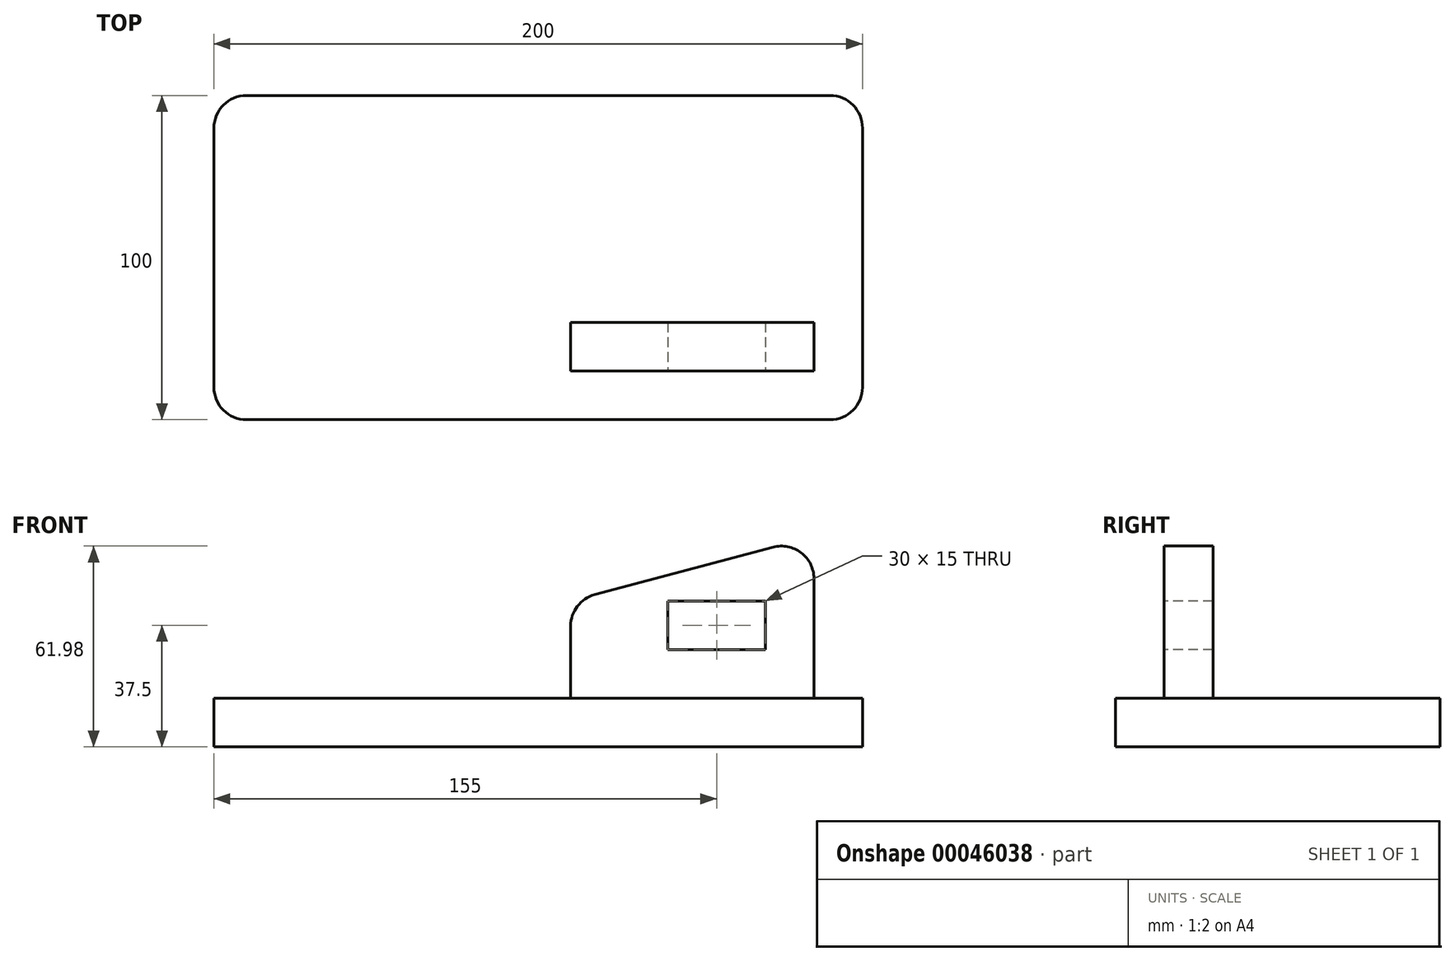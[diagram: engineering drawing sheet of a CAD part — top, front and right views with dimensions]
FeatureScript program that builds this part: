
annotation { "Feature Type Name" : "Feature", "Feature Type Description" : "" }
export const myFeature = defineFeature(function(context is Context, id is Id, definition is map)
    precondition{}
    {
        {
            var Q0;
            Q0=qCreatedBy(makeId("Top.planeOp"),FACE);
            var sketch = newSketch(context, id + "F0", { "sketchPlane" : qUnion([Q0])});
            skLineSegment(sketch, "E0.rect.bottom", {"start": v(100, -50) * mm, "end": v(-100, -50) * mm});
            skLineSegment(sketch, "E0.rect.top", {"start": v(100, 50) * mm, "end": v(-100, 50) * mm});
            skLineSegment(sketch, "E0.rect.left", {"start": v(100, -50) * mm, "end": v(100, 50) * mm});
            skLineSegment(sketch, "E0.rect.right", {"start": v(-100, -50) * mm, "end": v(-100, 50) * mm});
            skPoint(sketch, "E0.rect.middle", {"position": v(0, 0) * mm});
            skSolve(sketch);
        }
        {
            var Q0;
            Q0=makeQuery(id+"F0.imprint","IMPRINT",FACE,{"disambiguationData":[TD([[makeQuery(id+"F0.imprint","IMPRINT",EDGE,{"derivedFrom":sQuery(id+"F0.wireOp",EDGE,"E0.rect.bottom")}),-1.0]])]});
            extrude(context, id + "F1", {"entities" : qUnion([Q0]), "depth" : 15 * mm});
        }
        {
            var Q0;
            Q0=makeQuery(id+"F1.opExtrude","SWEPT_FACE",FACE,{"disambiguationData":[OSD([sQuery(id+"F0.wireOp",EDGE,"E0.rect.bottom")])]});
            cPlane(context, id + "F2", {"entities" : qUnion([Q0]), "cplaneType" : CPlaneType.OFFSET, "offset" : 15 * mm, "oppositeDirection" : true, "width" : 150 * mm, "height" : 150 * mm});
        }
        {
            var Q0;
            Q0=qCreatedBy(id+"F2.planeOp",FACE);
            var sketch = newSketch(context, id + "F3", { "sketchPlane" : qUnion([Q0])});
            skLineSegment(sketch, "E1", {"start": v(85, 15) * mm, "end": v(85, 65) * mm});
            skLineSegment(sketch, "E2", {"start": v(85, 65) * mm, "end": v(10, 45) * mm});
            skLineSegment(sketch, "E3", {"start": v(10, 45) * mm, "end": v(10, 15) * mm});
            skLineSegment(sketch, "E4", {"start": v(10, 15) * mm, "end": v(85, 15) * mm});
            skSolve(sketch);
        }
        {
            var Q0;
            Q0=makeQuery(id+"F3.imprint","IMPRINT",FACE,{"disambiguationData":[TD([[makeQuery(id+"F3.imprint","IMPRINT",EDGE,{"derivedFrom":sQuery(id+"F3.wireOp",EDGE,"E1")}),1.0]])]});
            extrude(context, id + "F4", {"entities" : qUnion([Q0]), "operationType" : NewBodyOperationType.ADD, "oppositeDirection" : true, "depth" : 15 * mm});
        }
        {
            var Q0;
            Q0=makeQuery(id+"F4.opExtrude","CAP_FACE",FACE,{"disambiguationData":[OSD([sQuery(id+"F3.wireOp",EDGE,"E1"),sQuery(id+"F3.wireOp",EDGE,"E2"),sQuery(id+"F3.wireOp",EDGE,"E3"),sQuery(id+"F3.wireOp",EDGE,"E4")])],"isStart":true});
            var sketch = newSketch(context, id + "F5", { "sketchPlane" : qUnion([Q0])});
            skLineSegment(sketch, "E5.bottom", {"start": v(70, 30) * mm, "end": v(40, 30) * mm});
            skLineSegment(sketch, "E5.top", {"start": v(70, 45) * mm, "end": v(40, 45) * mm});
            skLineSegment(sketch, "E5.left", {"start": v(70, 30) * mm, "end": v(70, 45) * mm});
            skLineSegment(sketch, "E5.right", {"start": v(40, 30) * mm, "end": v(40, 45) * mm});
            skSolve(sketch);
        }
        {
            var Q0;
            Q0=makeQuery(id+"F5.imprint","IMPRINT",FACE,{"disambiguationData":[TD([[makeQuery(id+"F5.imprint","IMPRINT",EDGE,{"derivedFrom":sQuery(id+"F5.wireOp",EDGE,"E5.bottom")}),-1.0]])]});
            extrude(context, id + "F6", {"entities" : qUnion([Q0]), "operationType" : NewBodyOperationType.REMOVE, "endBound" : BoundingType.UP_TO_NEXT, "oppositeDirection" : true, "depth" : 25 * mm});
        }
        {
            var Q0;
            Q0=makeQuery(id+"F4.opExtrude","SWEPT_EDGE",EDGE,{"disambiguationData":[OSD([sQuery(id+"F3.wireOp",EDGE,"E2"),sQuery(id+"F3.wireOp",EDGE,"E3")])]});
            var Q1;
            Q1=makeQuery(id+"F4.opExtrude","SWEPT_EDGE",EDGE,{"disambiguationData":[OSD([sQuery(id+"F3.wireOp",EDGE,"E1"),sQuery(id+"F3.wireOp",EDGE,"E2")])]});
            var Q2;
            Q2=makeQuery(id+"F1.opExtrude","SWEPT_EDGE",EDGE,{"disambiguationData":[OSD([sQuery(id+"F0.wireOp",EDGE,"E0.rect.bottom"),sQuery(id+"F0.wireOp",EDGE,"E0.rect.left")])]});
            var Q3;
            Q3=makeQuery(id+"F1.opExtrude","SWEPT_EDGE",EDGE,{"disambiguationData":[OSD([sQuery(id+"F0.wireOp",EDGE,"E0.rect.bottom"),sQuery(id+"F0.wireOp",EDGE,"E0.rect.right")])]});
            var Q4;
            Q4=makeQuery(id+"F1.opExtrude","SWEPT_EDGE",EDGE,{"disambiguationData":[OSD([sQuery(id+"F0.wireOp",EDGE,"E0.rect.top"),sQuery(id+"F0.wireOp",EDGE,"E0.rect.right")])]});
            var Q5;
            Q5=makeQuery(id+"F1.opExtrude","SWEPT_EDGE",EDGE,{"disambiguationData":[OSD([sQuery(id+"F0.wireOp",EDGE,"E0.rect.top"),sQuery(id+"F0.wireOp",EDGE,"E0.rect.left")])]});
            fillet(context, id + "F7", {"entities" : qUnion([Q0, Q1, Q2, Q3, Q4, Q5]), "radius" : 10 * mm, "tangentPropagation" : true, "allowEdgeOverflow" : false});
        }
    });
